# Revit family: 换热机组 - 0.5-4.0 MW
name_source: partatom
category: 机械设备
units: mm (PartAtom-declared; Revit-internal decimal feet)

## family parameters
共享 = 否
加载时剪切的空心 = 否
圆形连接件大小 = 使用半径
基于工作平面 = 否
总是垂直 = 是
房间计算点 = 否
零件类型 = 标准

## types (3) — shared parameters
一次水出口温度 = 80 °C
一次水进口温度 = 130 °C
二次水出口温度 = 70 °C
二次水进口温度 = 95 °C
半径 10 = 10  [stored 0.0328084 ft]
半径 5 = 30  [stored 0.0984252 ft]
半径 6 = 35  [stored 0.114829 ft]
半径 7 = 80  [stored 0.262467 ft]
半径 8 = 30  [stored 0.0984252 ft]
极数 = 3
法兰厚度 = 10  [stored 0.0328084 ft]
热交换器材质 = <按类别>
电压 = 380 V
角度 = 45.00°
负荷分类 = 采暖
zero-valued in all types: 默认高程

## per-type parameters (varying)
- 0.50-1.25 MW: 一次水出口半径=40 mm; 一次水出口法兰半径=60  [stored 0.19685 ft]; 一次水出口法兰直径=120  [stored 0.393701 ft]; 一次水出口直径=80 mm; 一次水进口半径=40 mm; 一次水进口法兰半径=60  [stored 0.19685 ft]; 一次水进口法兰直径=120  [stored 0.393701 ft]; 一次水进口直径=80 mm; 供水半径=50 mm; 供水法兰半径=75; 供水法兰直径=150; 供水直径=100 mm; 半径 1=125  [stored 0.410105 ft]; 半径 2=118; 半径 3=150; 半径 4=38  [stored 0.124672 ft]; 半径 9=48  [stored 0.15748 ft]; 回水半径=50 mm; 回水法兰半径=75; 回水法兰直径=150; 回水直径=100 mm; 型号=0.5-1.25MW; 宽度 1=232; 宽度 2=280; 宽度 3=118; 宽度 4=471; 宽度 5=64  [stored 0.209974 ft]; 宽度 6=235; 宽度 7=353; 宽度 8=88; 局部阻力系数=0.200 mm; 换热量=1250.00 kW; 热交换器宽度=1177; 热交换器长度=2526; 热交换器高度=1800; 管道状态=正常; 粗糙系数=0.200 mm; 补水管半径=13 mm; 补水管法兰半径=38  [stored 0.124672 ft]; 补水管法兰直径=75; 补水管直径=25 mm; 视在负荷=15.00 kW; 重量=1500 kg; 长度 1=320; 长度 2=2056; 长度 3=411; 长度 4=51; 长度 5=206; 长度 6=103; 高度 1=1080; 高度 2=280; 高度 3=175; 高度 4=88
- 1.00-2.50 MW: 一次水出口半径=50 mm; 一次水出口法兰半径=75; 一次水出口法兰直径=150; 一次水出口直径=100 mm; 一次水进口半径=50 mm; 一次水进口法兰半径=75; 一次水进口法兰直径=150; 一次水进口直径=100 mm; 供水半径=63 mm; 供水法兰半径=94; 供水法兰直径=188; 供水直径=125 mm; 半径 1=139; 半径 2=132; 半径 3=188; 半径 4=48  [stored 0.15748 ft]; 半径 9=60  [stored 0.19685 ft]; 回水半径=63 mm; 回水法兰半径=94; 回水法兰直径=188; 回水直径=125 mm; 宽度 1=124; 宽度 2=497; 宽度 3=132; 宽度 4=528; 宽度 5=80  [stored 0.262467 ft]; 宽度 6=264; 宽度 7=396; 宽度 8=99; 局部阻力系数=0.000 mm; 换热量=2500.00 kW; 热交换器宽度=1321; 热交换器长度=2803; 热交换器高度=1900; 粗糙系数=0.000 mm; 补水管半径=16 mm; 补水管法兰半径=48  [stored 0.15748 ft]; 补水管法兰直径=96  [stored 0.314961 ft]; 补水管直径=32 mm; 视在负荷=30.00 kW; 重量=2500 kg; 长度 1=320; 长度 2=2340; 长度 3=468; 长度 4=56; 长度 5=234; 长度 6=117; 高度 1=1040; 高度 2=325; 高度 3=175; 高度 4=88
- 2.00-4.00 MW: 一次水出口半径=63 mm; 一次水出口法兰半径=94; 一次水出口法兰直径=188; 一次水出口直径=125 mm; 一次水进口半径=63 mm; 一次水进口法兰半径=94; 一次水进口法兰直径=188; 一次水进口直径=125 mm; 供水半径=75 mm; 供水法兰半径=113; 供水法兰直径=225  [stored 0.738189 ft]; 供水直径=150 mm; 半径 1=175; 半径 2=160  [stored 0.524934 ft]; 半径 3=225  [stored 0.738189 ft]; 半径 4=60  [stored 0.19685 ft]; 半径 9=75; 回水半径=75 mm; 回水法兰半径=113; 回水法兰直径=225  [stored 0.738189 ft]; 回水直径=150 mm; 宽度 1=123; 宽度 2=583; 宽度 3=160  [stored 0.524934 ft]; 宽度 4=638; 宽度 5=100  [stored 0.328084 ft]; 宽度 6=319; 宽度 7=479; 宽度 8=120  [stored 0.393701 ft]; 局部阻力系数=0.000 mm; 换热量=4000.00 kW; 热交换器宽度=1596; 热交换器长度=3370; 热交换器高度=2000; 粗糙系数=0.000 mm; 补水管半径=20 mm; 补水管法兰半径=60  [stored 0.19685 ft]; 补水管法兰直径=120  [stored 0.393701 ft]; 补水管直径=40 mm; 视在负荷=45.00 kW; 重量=3500 kg; 长度 1=381; 长度 2=2880; 长度 3=576; 长度 4=67; 长度 5=288; 长度 6=144; 高度 1=710; 高度 2=526; 高度 3=195; 高度 4=98

note: [stored X ft] marks values corroborated as IEEE doubles in the binary element streams (Revit-internal decimal feet)
